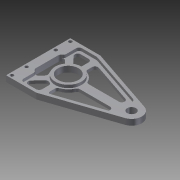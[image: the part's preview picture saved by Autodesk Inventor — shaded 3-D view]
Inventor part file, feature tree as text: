
AUTODESK INVENTOR PART (.ipt)
format: ipt  version: 2012 (Build 160160000, 160)  size: 258,560 bytes
history: native  units: in
note: dims shown in document units (in); Inventor stores cm internally (conversion verified against a paired STEP export)
features: extrude x3, fillet x3, sketch x2, hole x1
ambient origin geometry x8: Origin, YZ Plane, XZ Plane, XY Plane, X Axis, Y Axis, Z Axis, Center Point
bodies: Solid1 (feature_tree)
feature tree (9):
  sketch  "Sketch1"  dims[d0=2.75in d1=4.0in]
  extrude  "Extrusion1"  Depth=4.0in
  extrude  "Extrusion2"  Depth=0.1279in
  fillet  "Fillet1"  Radius=0.375in
  hole  "Hole1"  [1 undecoded]
  sketch  "Sketch2"  dims[d2=1.375in d6=0.1279in d7=0.375in d8=1.289in d9=0.875in d10=0.125in d11=0.0in d12=0.625in d13=0.1875in d14=0.1875in d15=0.25in d16=0.25in d17=0.125in d18=0.125in d19=0.125in d20=0.125in d21=0.125in d22=0.125in d24=0.125in d25=0.125in d26=0.25in d27=0.375in d28=0.25in d29=0.125in d30=0.0in d31=0.125in d32=0.125in d33=0.125in d35=0.125in d36=0.125in d38=0.144in d39=0.75in d40=0.25in d41=0.25in d42=0.5635in d43=1.0in d44=0.8108in d45=0.5in d46=0.125in d47=0.125in d48=0.125in d49=0.125in d51=0.125in d53=0.875in d54=0.0625in d58=0.125in d59=0.0in d62=0.75in d63=0.75in d69=0.125in d70=0.1279in d71=0.4375in d72=1.125in d73=0.125in d74=0.125in]
  extrude  "Extrusion4"  Depth=0.875in
  fillet  "Fillet6"  Radius=0.125in
  fillet  "Fillet7"  Radius=0.625in
note: 1 required parameter value undecoded (feature->parameter linkage not recoverable at this tier; creation-order binding heuristic only, values carry confidence <= 0.55)
